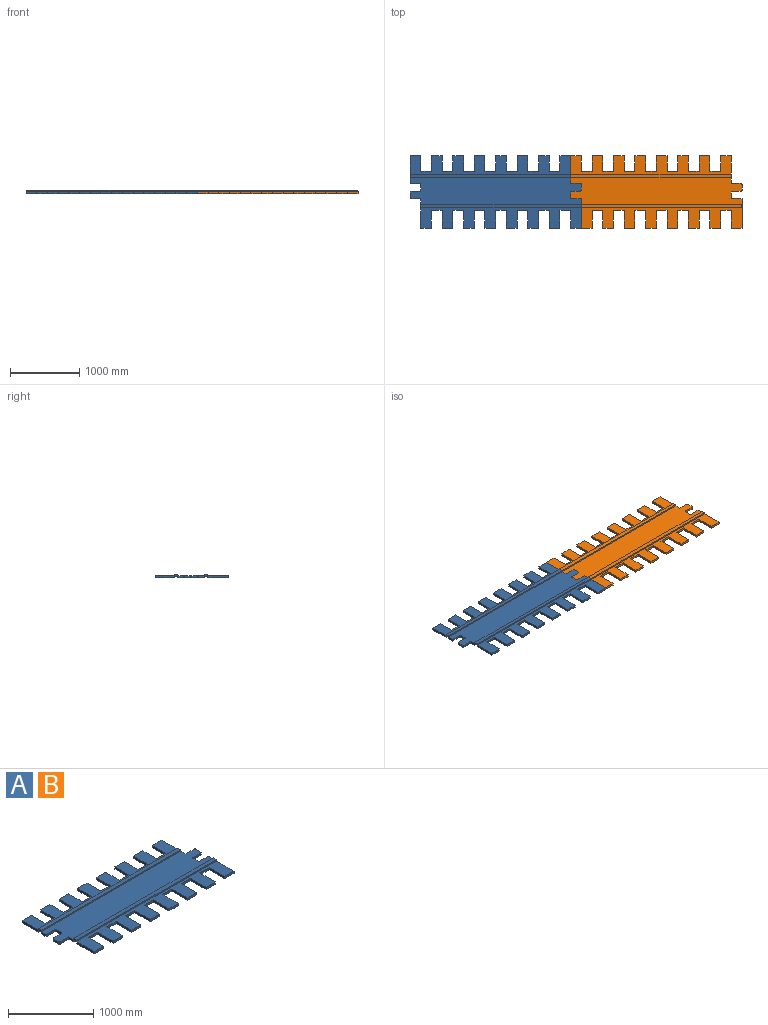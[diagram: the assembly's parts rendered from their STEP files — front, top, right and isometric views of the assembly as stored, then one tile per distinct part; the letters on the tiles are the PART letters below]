
ASSEMBLY  parts=2 mates=1
PART A: 105 faces, bbox 2469.2x1048.8x50.8 mm
  f0: plane 2314.58x269.05mm, normal (0,0,-1), area 375079.1mm2, adj f7,f8,f9,f10,f11,f12,f13,f14
  f1: plane 2468.9x383.6mm, normal (0,0,-1), area 887869.2mm2, adj f2,f4,f5,f31,f32,f33,f34,f35
  f2: plane 427.85x31.75mm, normal (1,0,0), area 12294.1mm2, adj f1,f6,f69,f70,f88,f99,f100,f101
  f3: plane 294.58x31.75mm, normal (-1,0,0), area 9353.1mm2, adj f6,f41,f88,f97,f99
  f4: plane 81.11x31.75mm, normal (-1,0,0), area 2575.3mm2, adj f1,f6,f31,f90,f102
  f5: plane 81.11x31.75mm, normal (1,0,0), area 2575.3mm2, adj f1,f6,f78,f90,f102
  f6: plane 2468.9x728.98mm, normal (0,0,1), area 1290989.8mm2, adj f2,f3,f4,f5,f31,f32,f33,f34
  f7: plane 154.31x31.75mm, normal (0,1,0), area 4899.2mm2, adj f0,f8,f86,f87
  f8: plane 228.83x31.75mm, normal (1,0,0), area 7265.3mm2, adj f0,f7,f9,f87
  f9: plane 154.31x31.75mm, normal (0,1,0), area 4899.2mm2, adj f0,f8,f10,f87
  f10: plane 228.83x31.75mm, normal (-1,0,0), area 7265.3mm2, adj f0,f9,f11,f87
  f11: plane 154.31x31.75mm, normal (0,1,0), area 4899.2mm2, adj f0,f10,f12,f87
  f12: plane 228.83x31.75mm, normal (1,0,0), area 7265.3mm2, adj f0,f11,f13,f87
  f13: plane 154.31x31.75mm, normal (0,1,0), area 4899.2mm2, adj f0,f12,f14,f87
  f14: plane 228.83x31.75mm, normal (-1,0,0), area 7265.3mm2, adj f0,f13,f15,f87
  f15: plane 154.31x31.75mm, normal (0,1,0), area 4899.2mm2, adj f0,f14,f16,f87
  f16: plane 228.83x31.75mm, normal (1,0,0), area 7265.3mm2, adj f0,f15,f17,f87
  f17: plane 154.31x31.75mm, normal (0,1,0), area 4899.2mm2, adj f0,f16,f18,f87
  f18: plane 228.83x31.75mm, normal (-1,0,0), area 7265.3mm2, adj f0,f17,f19,f87
  f19: plane 154.31x31.75mm, normal (0,1,0), area 4899.2mm2, adj f0,f18,f20,f87
  f20: plane 227.75x31.75mm, normal (1,0,0), area 7231mm2, adj f0,f19,f21,f87
  f21: plane 154.31x31.75mm, normal (0,1,0), area 4899.2mm2, adj f0,f20,f22,f87
  f22: plane 227.75x31.75mm, normal (-1,0,0), area 7231mm2, adj f0,f21,f23,f87
  f23: plane 154.31x31.75mm, normal (0,1,0), area 4899.2mm2, adj f0,f22,f24,f87
  f24: plane 227.75x31.75mm, normal (1,0,0), area 7231mm2, adj f0,f23,f25,f87
  f25: plane 154.31x31.75mm, normal (0,1,0), area 4899.2mm2, adj f0,f24,f26,f87
  f26: plane 227.75x31.75mm, normal (-1,0,0), area 7231mm2, adj f0,f25,f27,f87
  f27: plane 154.31x31.75mm, normal (0,1,0), area 4899.2mm2, adj f0,f26,f28,f87
  f28: plane 227.75x31.75mm, normal (1,0,0), area 7231mm2, adj f0,f27,f29,f87
  f29: plane 154.31x31.75mm, normal (0,1,0), area 4899.2mm2, adj f0,f28,f30,f87
  f30: plane 267.97x31.75mm, normal (-1,0,0), area 8508.1mm2, adj f0,f29,f87,f92,f103
  f31: plane 141.61x31.75mm, normal (0,-1,0), area 4496mm2, adj f1,f4,f6,f32
  f32: cylinder r=12.7mm len=31.75mm, axis (0,0,-1), area 633.4mm2, adj f1,f6,f31,f33
  f33: plane 84.61x31.75mm, normal (-1,0,0), area 2686.3mm2, adj f1,f6,f32,f34
  f34: cylinder r=12.7mm len=31.75mm, axis (0,0,-1), area 633.4mm2, adj f1,f6,f33,f35
  f35: plane 128.91x31.75mm, normal (0,1,0), area 4092.7mm2, adj f1,f6,f34,f36
  f36: cylinder r=12.7mm len=31.75mm, axis (0,0,-1), area 633.4mm2, adj f1,f6,f35,f37
  f37: plane 84.61x31.75mm, normal (-1,0,0), area 2686.3mm2, adj f1,f6,f36,f38
  f38: cylinder r=12.7mm len=31.75mm, axis (0,0,-1), area 633.4mm2, adj f1,f6,f37,f39
  f39: plane 141.61x31.75mm, normal (0,-1,0), area 4496mm2, adj f1,f6,f38,f40
  f40: plane 82.47x31.75mm, normal (-1,0,0), area 2618.4mm2, adj f1,f6,f39,f95,f100
  f41: plane 154.31x31.75mm, normal (0,-1,0), area 4899.5mm2, adj f3,f6,f42,f88
  f42: plane 258.05x31.75mm, normal (1,0,0), area 8193.2mm2, adj f6,f41,f43,f88
  f43: plane 154.31x31.75mm, normal (0,-1,0), area 4899.2mm2, adj f6,f42,f44,f88
  f44: plane 258.05x31.75mm, normal (-1,0,0), area 8193.2mm2, adj f6,f43,f45,f88
  f45: plane 154.31x31.75mm, normal (0,-1,0), area 4899.5mm2, adj f6,f44,f46,f88
  f46: plane 258.05x31.75mm, normal (1,0,0), area 8193.2mm2, adj f6,f45,f47,f88
  f47: plane 154.31x31.75mm, normal (0,-1,0), area 4899.2mm2, adj f6,f46,f48,f88
  f48: plane 258.05x31.75mm, normal (-1,0,0), area 8193.2mm2, adj f6,f47,f49,f88
  f49: plane 154.31x31.75mm, normal (0,-1,0), area 4899.2mm2, adj f6,f48,f50,f88
  f50: plane 258.05x31.75mm, normal (1,0,0), area 8193.2mm2, adj f6,f49,f51,f88
  f51: plane 154.31x31.75mm, normal (0,-1,0), area 4899.2mm2, adj f6,f50,f52,f88
  f52: plane 258.05x31.75mm, normal (-1,0,0), area 8193.2mm2, adj f6,f51,f53,f88
  f53: plane 154.31x31.75mm, normal (0,-1,0), area 4899.2mm2, adj f6,f52,f54,f88
  f54: plane 258.05x31.75mm, normal (1,0,0), area 8193.2mm2, adj f6,f53,f55,f88
  f55: plane 154.31x31.75mm, normal (0,-1,0), area 4899.2mm2, adj f6,f54,f56,f88
  f56: plane 258.05x31.75mm, normal (-1,0,0), area 8193.2mm2, adj f6,f55,f57,f88
  f57: plane 154.31x31.75mm, normal (0,-1,0), area 4899.2mm2, adj f6,f56,f58,f88
  f58: plane 258.05x31.75mm, normal (1,0,0), area 8193.2mm2, adj f6,f57,f59,f88
  f59: plane 154.31x31.75mm, normal (0,-1,0), area 4899.2mm2, adj f6,f58,f60,f88
  f60: plane 258.05x31.75mm, normal (-1,0,0), area 8193.2mm2, adj f6,f59,f61,f88
  f61: plane 154.31x31.75mm, normal (0,-1,0), area 4899.2mm2, adj f6,f60,f62,f88
  f62: plane 258.05x31.75mm, normal (1,0,0), area 8193.2mm2, adj f6,f61,f63,f88
  f63: plane 154.31x31.75mm, normal (0,-1,0), area 4899.2mm2, adj f6,f62,f64,f88
  f64: plane 258.05x31.75mm, normal (-1,0,0), area 8193.2mm2, adj f6,f63,f65,f88
  f65: plane 154.31x31.75mm, normal (0,-1,0), area 4899.2mm2, adj f6,f64,f66,f88
  f66: plane 258.05x31.75mm, normal (1,0,0), area 8193.2mm2, adj f6,f65,f67,f88
  f67: plane 154.31x31.75mm, normal (0,-1,0), area 4899.2mm2, adj f6,f66,f68,f88
  f68: plane 258.05x31.75mm, normal (-1,0,0), area 8193.2mm2, adj f6,f67,f69,f88
  f69: plane 154.31x31.75mm, normal (0,-1,0), area 4899.2mm2, adj f2,f6,f68,f88
  f70: plane 141.61x31.75mm, normal (0,1,0), area 4496mm2, adj f1,f2,f6,f71
  f71: cylinder r=12.7mm len=31.75mm, axis (0,0,-1), area 633.4mm2, adj f1,f6,f70,f72
  f72: plane 84.61x31.75mm, normal (1,0,0), area 2686.3mm2, adj f1,f6,f71,f73
  f73: cylinder r=12.7mm len=31.75mm, axis (0,0,-1), area 633.4mm2, adj f1,f6,f72,f74
  f74: plane 128.91x31.75mm, normal (0,-1,0), area 4092.7mm2, adj f1,f6,f73,f75
  f75: cylinder r=12.7mm len=31.75mm, axis (0,0,-1), area 633.4mm2, adj f1,f6,f74,f76
  f76: plane 84.61x31.75mm, normal (1,0,0), area 2686.3mm2, adj f1,f6,f75,f77
  f77: cylinder r=12.7mm len=31.75mm, axis (0,0,-1), area 633.4mm2, adj f1,f6,f76,f78
  f78: plane 141.61x31.75mm, normal (0,1,0), area 4496mm2, adj f1,f5,f6,f77
  f79: plane 40.23x31.75mm, normal (1,0,0), area 1277.1mm2, adj f0,f80,f87,f92,f103
  f80: plane 228.83x31.75mm, normal (1,0,0), area 7265.3mm2, adj f0,f79,f81,f87
  f81: plane 154.31x31.75mm, normal (0,1,0), area 4899.2mm2, adj f0,f80,f82,f87
  f82: plane 228.83x31.75mm, normal (-1,0,0), area 7265.3mm2, adj f0,f81,f83,f87
  f83: plane 154.31x31.75mm, normal (0,1,0), area 4899.2mm2, adj f0,f82,f84,f87
  f84: plane 228.83x31.75mm, normal (1,0,0), area 7265.3mm2, adj f0,f83,f85,f87
  f85: plane 154.31x31.75mm, normal (0,1,0), area 4899.2mm2, adj f0,f84,f86,f87
  f86: plane 228.83x31.75mm, normal (-1,0,0), area 7265.3mm2, adj f0,f7,f85,f87
  f87: plane 2314.58x269.05mm, normal (0,0,1), area 375079.1mm2, adj f7,f8,f9,f10,f11,f12,f13,f14
  f88: plane 2314.59x294.58mm, normal (0,0,-1), area 403111.1mm2, adj f2,f3,f41,f42,f43,f44,f45,f46
  f89: plane 50.8x25.4mm, normal (-1,0,0), area 1290.3mm2, adj f90,f92,f93,f104
  f90: plane 2314.86x25.4mm, normal (0,-1,0), area 44099.9mm2, adj f4,f5,f6,f89,f91,f93,f104
  f91: plane 50.8x25.4mm, normal (1,0,0), area 1290.3mm2, adj f90,f92,f93,f104
  f92: plane 2314.86x25.4mm, normal (0,1,0), area 44099.9mm2, adj f30,f79,f87,f89,f91,f93,f104
  f93: plane 2314.86x50.8mm, normal (0,0,1), area 117595mm2, adj f89,f90,f91,f92
  f94: plane 50.8x19.05mm, normal (1,0,0), area 967.7mm2, adj f6,f95,f97,f98
  f95: plane 2314.7x25.4mm, normal (0,1,0), area 44097mm2, adj f6,f40,f94,f96,f98,f101
  f96: plane 50.8x25.4mm, normal (-1,0,0), area 1290.3mm2, adj f95,f97,f98,f101
  f97: plane 2314.7x25.4mm, normal (0,-1,0), area 44097mm2, adj f3,f6,f94,f96,f98,f101
  f98: plane 2314.7x50.8mm, normal (0,0,1), area 117586.9mm2, adj f94,f95,f96,f97
  f99: plane 2314.59x25.4mm, normal (0,1,0), area 58790.6mm2, adj f2,f3,f88,f101
  f100: plane 2314.59x25.4mm, normal (0,-1,0), area 58790.6mm2, adj f1,f2,f40,f101
  f101: plane 2314.89x50.8mm, normal (0,0,-1), area 117596.5mm2, adj f2,f95,f96,f97,f99,f100
  f102: plane 2314.58x25.4mm, normal (0,1,0), area 58790.4mm2, adj f1,f4,f5,f104
  f103: plane 2314.58x25.4mm, normal (0,-1,0), area 58790.3mm2, adj f0,f30,f79,f104
  f104: plane 2314.86x50.8mm, normal (0,0,-1), area 117595mm2, adj f89,f90,f91,f92,f102,f103
PART B: same geometry as A
PLACE A t=(153.58,127.5,783.21)mm
PLACE B t=(2468.17,127.5,783.21)mm
MATE fastened B.f37 <-> A.f72  axis (-1,0,0) through (153.58,-37.51,799.09)mm
